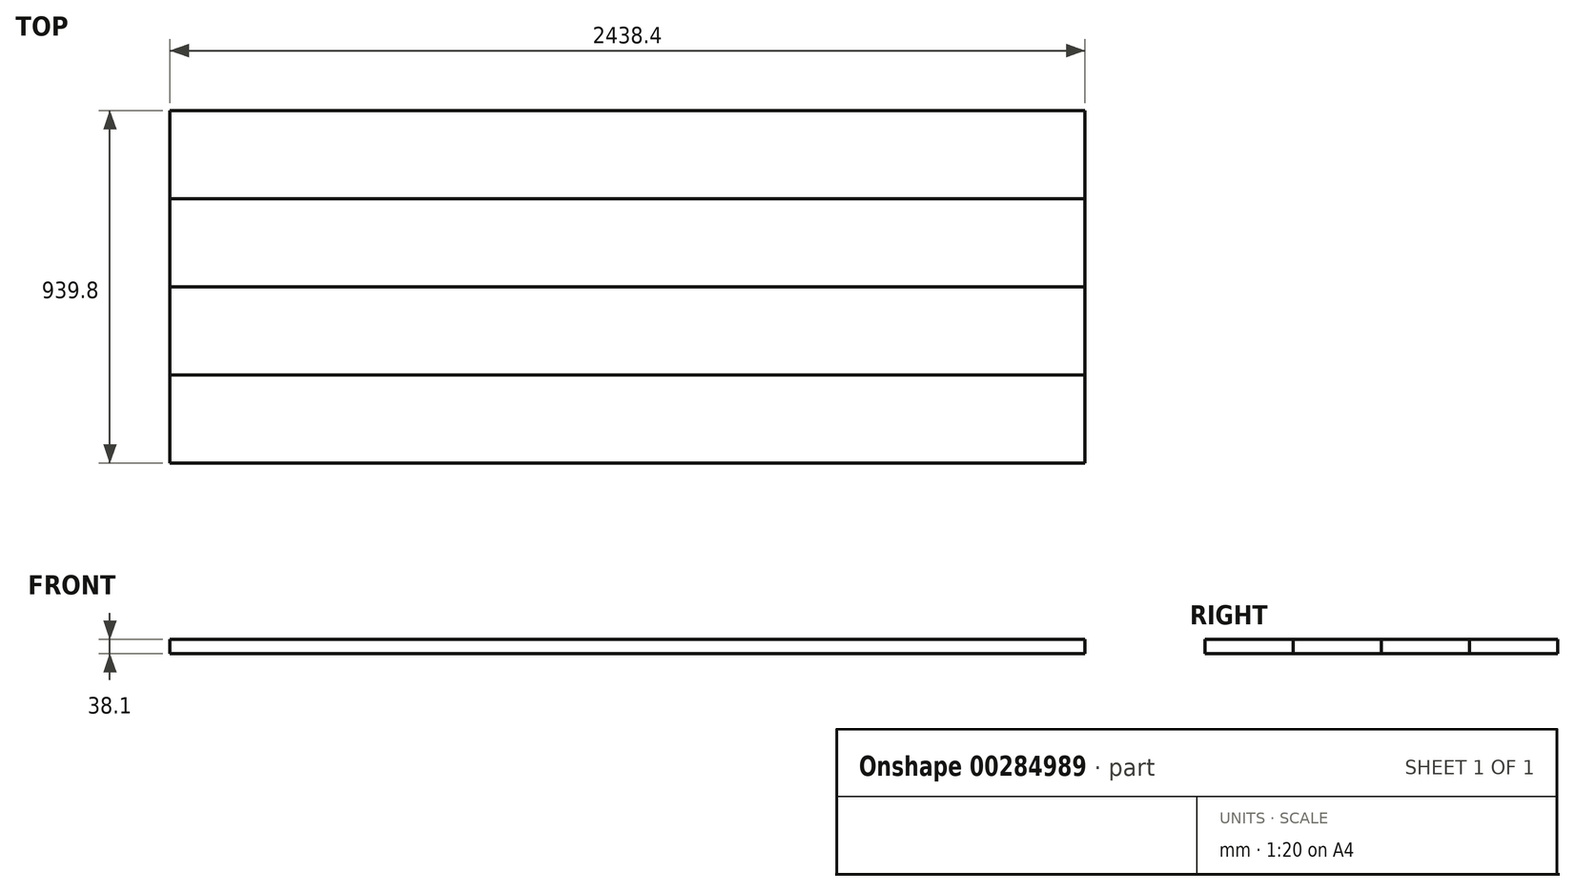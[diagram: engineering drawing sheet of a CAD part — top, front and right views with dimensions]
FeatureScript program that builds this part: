
annotation { "Feature Type Name" : "Feature", "Feature Type Description" : "" }
export const myFeature = defineFeature(function(context is Context, id is Id, definition is map)
    precondition{}
    {
        {
            var Q0;
            Q0=qCreatedBy(makeId("Top.planeOp"),FACE);
            var sketch = newSketch(context, id + "F0", { "sketchPlane" : qUnion([Q0])});
            skLineSegment(sketch, "E0.bottom", {"start": v(0, 0) * mm, "end": v(2438.4, 0) * mm});
            skLineSegment(sketch, "E0.top", {"start": v(0, 234.95) * mm, "end": v(2438.4, 234.95) * mm});
            skLineSegment(sketch, "E0.left", {"start": v(0, 0) * mm, "end": v(0, 234.95) * mm});
            skLineSegment(sketch, "E0.right", {"start": v(2438.4, 0) * mm, "end": v(2438.4, 234.95) * mm});
            skSolve(sketch);
        }
        {
            var Q0;
            Q0=makeQuery(id+"F0.imprint","IMPRINT",FACE,{"disambiguationData":[TD([[makeQuery(id+"F0.imprint","IMPRINT",EDGE,{"derivedFrom":sQuery(id+"F0.wireOp",EDGE,"E0.bottom")}),1.0]])]});
            extrude(context, id + "F1", {"entities" : qUnion([Q0]), "depth" : 38.1 * mm});
        }
        {
            var Q0;
            Q0=makeQuery(id+"F1.opExtrude","SWEPT_BODY",BODY,{"disambiguationData":[OSD([sQuery(id+"F0.wireOp",EDGE,"E0.bottom"),sQuery(id+"F0.wireOp",EDGE,"E0.top"),sQuery(id+"F0.wireOp",EDGE,"E0.left"),sQuery(id+"F0.wireOp",EDGE,"E0.right")])]});
            var Q1;
            Q1=makeQuery(id+"F1.opExtrude","SWEPT_FACE",FACE,{"disambiguationData":[OSD([sQuery(id+"F0.wireOp",EDGE,"E0.top")])]});
            mirror(context, id + "F2", {"entities" : qUnion([Q0]), "mirrorPlane" : qUnion([Q1])});
        }
        {
            var Q0;
            Q0=makeQuery(id+"F2.opPattern","COPY",BODY,{"derivedFrom":makeQuery(id+"F1.opExtrude","SWEPT_BODY",BODY,{"disambiguationData":[OSD([sQuery(id+"F0.wireOp",EDGE,"E0.bottom"),sQuery(id+"F0.wireOp",EDGE,"E0.top"),sQuery(id+"F0.wireOp",EDGE,"E0.left"),sQuery(id+"F0.wireOp",EDGE,"E0.right")])]}),"instanceName":"1"});
            var Q1;
            Q1=makeQuery(id+"F1.opExtrude","SWEPT_BODY",BODY,{"disambiguationData":[OSD([sQuery(id+"F0.wireOp",EDGE,"E0.bottom"),sQuery(id+"F0.wireOp",EDGE,"E0.top"),sQuery(id+"F0.wireOp",EDGE,"E0.left"),sQuery(id+"F0.wireOp",EDGE,"E0.right")])]});
            var Q2;
            Q2=makeQuery(id+"F2.opPattern","COPY",FACE,{"derivedFrom":makeQuery(id+"F1.opExtrude","SWEPT_FACE",FACE,{"disambiguationData":[OSD([sQuery(id+"F0.wireOp",EDGE,"E0.bottom")])]}),"instanceName":"1"});
            mirror(context, id + "F3", {"entities" : qUnion([Q0, Q1]), "mirrorPlane" : qUnion([Q2])});
        }
    });
